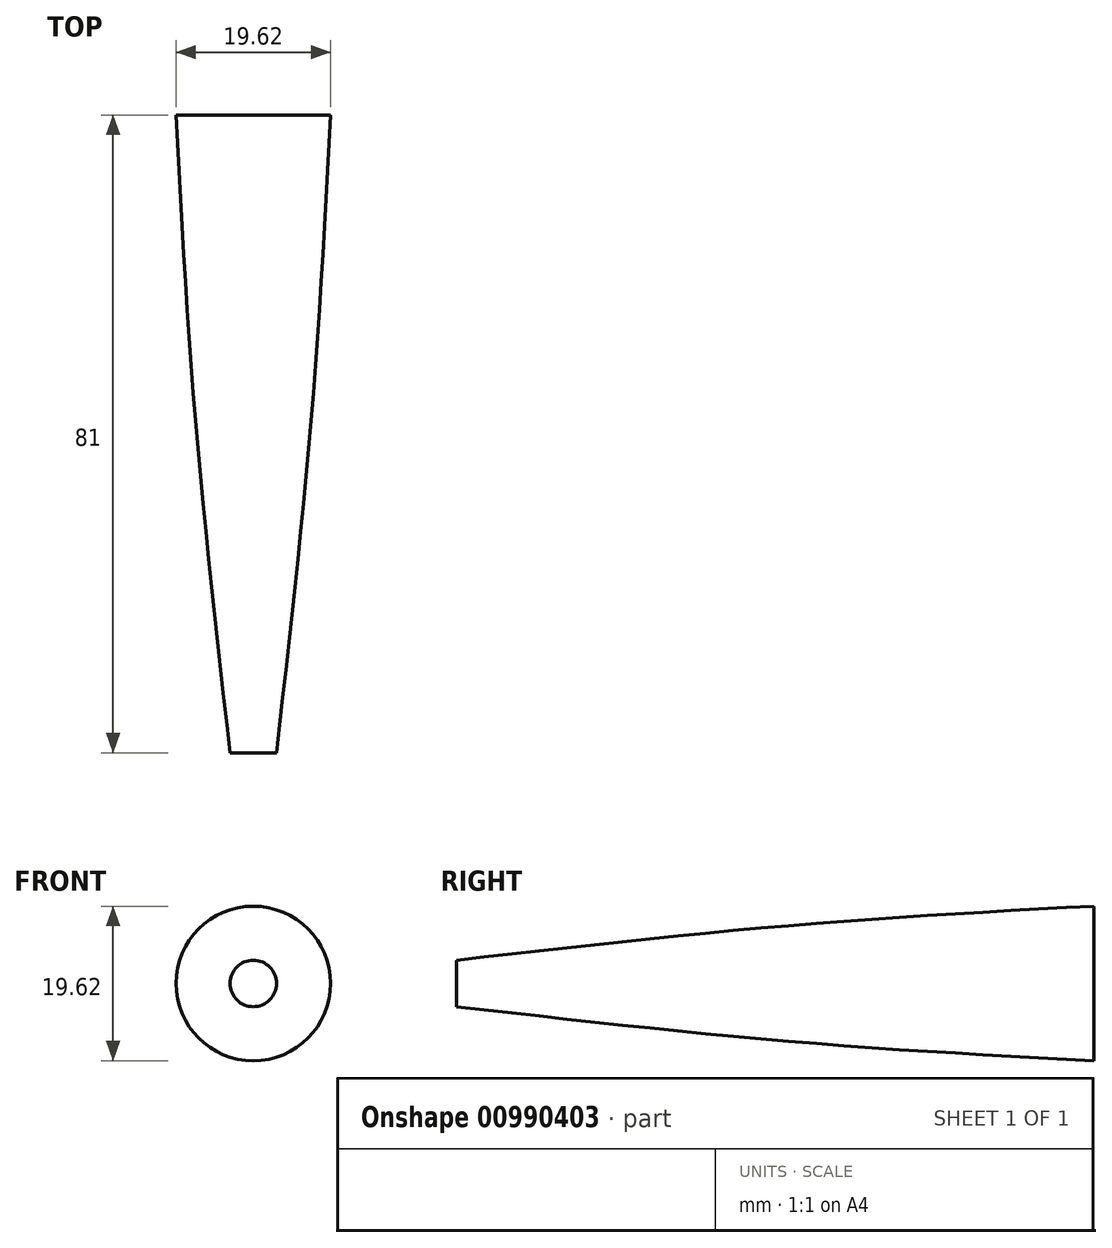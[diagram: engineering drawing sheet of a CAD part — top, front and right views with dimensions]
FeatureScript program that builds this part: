
annotation { "Feature Type Name" : "Feature", "Feature Type Description" : "" }
export const myFeature = defineFeature(function(context is Context, id is Id, definition is map)
    precondition{}
    {
        {
            var Q0;
            Q0=qCreatedBy(makeId("Front.planeOp"),FACE);
            var sketch = newSketch(context, id + "F0", { "sketchPlane" : qUnion([Q0])});
            skCircle(sketch, "E0", {"center": v(0, 0) * mm, "radius": 9.81 * mm});
            skSolve(sketch);
        }
        {
            var Q0;
            Q0=qCreatedBy(makeId("Front.planeOp"),FACE);
            cPlane(context, id + "F1", {"entities" : qUnion([Q0]), "cplaneType" : CPlaneType.OFFSET, "offset" : 33 * mm, "width" : 150 * mm, "height" : 150 * mm});
        }
        {
            var Q0;
            Q0=qCreatedBy(id+"F1.planeOp",FACE);
            var sketch = newSketch(context, id + "F2", { "sketchPlane" : qUnion([Q0])});
            skCircle(sketch, "E1", {"center": v(0, 0) * mm, "radius": 7.81 * mm});
            skSolve(sketch);
        }
        {
            var Q0;
            Q0=qCreatedBy(id+"F1.planeOp",FACE);
            cPlane(context, id + "F3", {"entities" : qUnion([Q0]), "cplaneType" : CPlaneType.OFFSET, "offset" : 48 * mm, "width" : 150 * mm, "height" : 150 * mm});
        }
        {
            var Q0;
            Q0=qCreatedBy(id+"F3.planeOp",FACE);
            var sketch = newSketch(context, id + "F4", { "sketchPlane" : qUnion([Q0])});
            skCircle(sketch, "E2", {"center": v(0, 0) * mm, "radius": 2.95 * mm});
            skSolve(sketch);
        }
        {
            var Q0;
            Q0=makeQuery(id+"F0.imprint","IMPRINT",FACE,{"disambiguationData":[TD([[makeQuery(id+"F0.imprint","IMPRINT",EDGE,{"derivedFrom":sQuery(id+"F0.wireOp",EDGE,"E0")}),1.0]])]});
            var Q1;
            Q1=makeQuery(id+"F2.imprint","IMPRINT",FACE,{"disambiguationData":[TD([[makeQuery(id+"F2.imprint","IMPRINT",EDGE,{"derivedFrom":sQuery(id+"F2.wireOp",EDGE,"E1")}),1.0]])]});
            var Q2;
            Q2=makeQuery(id+"F4.imprint","IMPRINT",FACE,{"disambiguationData":[TD([[makeQuery(id+"F4.imprint","IMPRINT",EDGE,{"derivedFrom":sQuery(id+"F4.wireOp",EDGE,"E2")}),1.0]])]});
            loft(context, id + "F5", {"sheetProfilesArray" : [{ "sheetProfileEntities" : qUnion([Q0]) }, { "sheetProfileEntities" : qUnion([Q1]) }, { "sheetProfileEntities" : qUnion([Q2]) }]});
        }
    });
